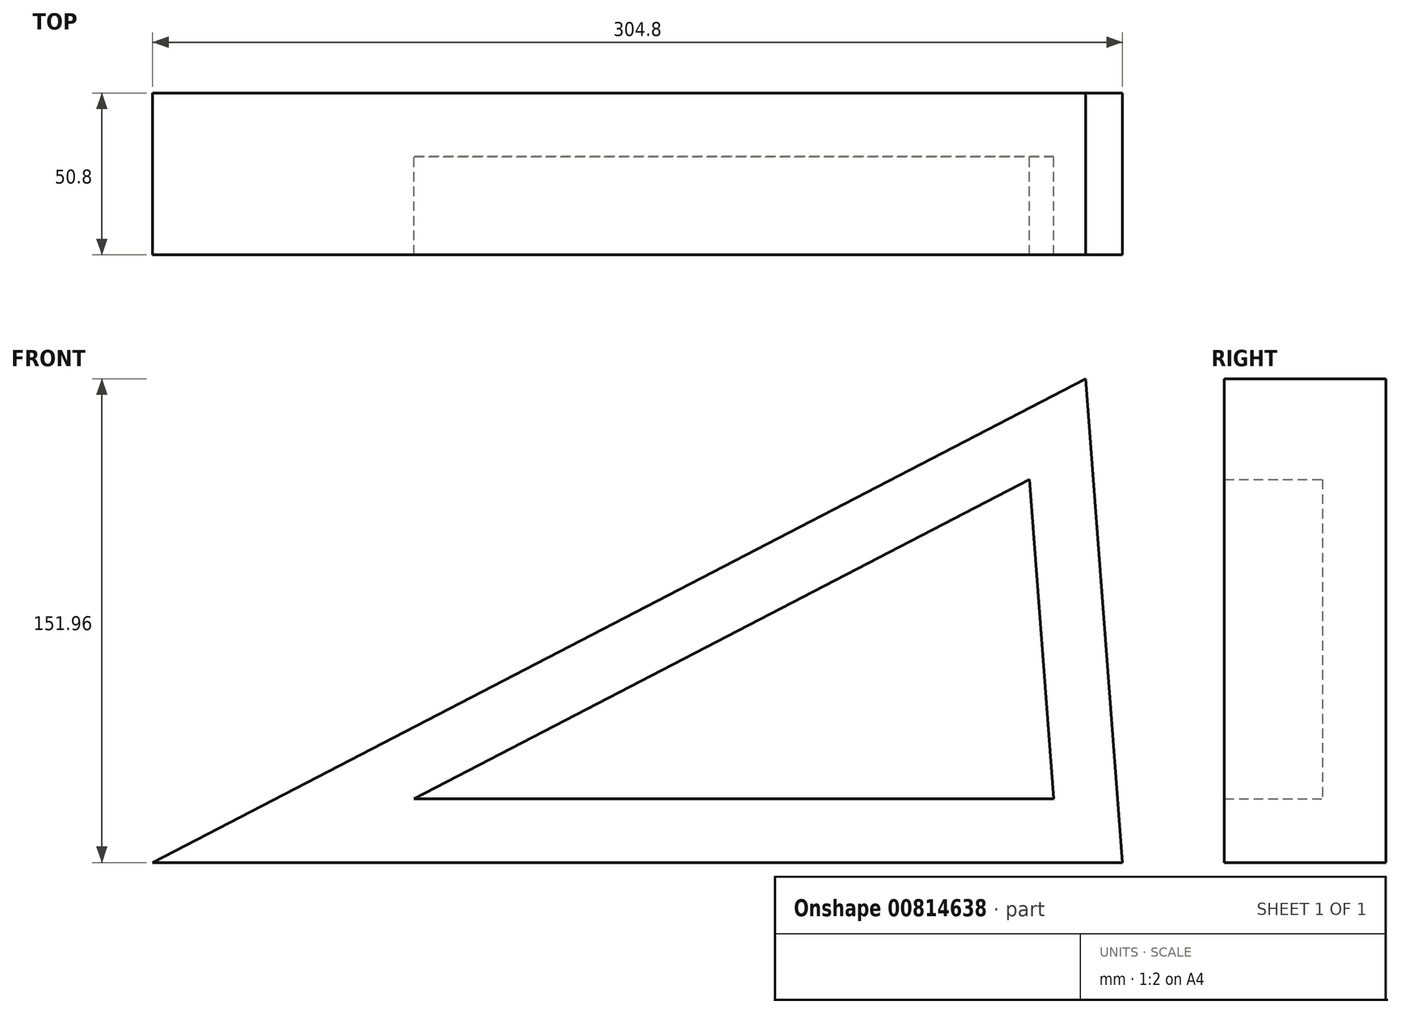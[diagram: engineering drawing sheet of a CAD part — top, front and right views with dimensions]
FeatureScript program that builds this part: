
annotation { "Feature Type Name" : "Feature", "Feature Type Description" : "" }
export const myFeature = defineFeature(function(context is Context, id is Id, definition is map)
    precondition{}
    {
        {
            var Q0;
            Q0=qCreatedBy(makeId("Front.planeOp"),FACE);
            var sketch = newSketch(context, id + "F0", { "sketchPlane" : qUnion([Q0])});
            skLineSegment(sketch, "E0.0", {"start": v(152.4, -87.99) * mm, "end": v(-152.4, -87.99) * mm});
            skLineSegment(sketch, "E0.1", {"start": v(-152.4, -87.99) * mm, "end": v(140.76, 63.97) * mm});
            skLineSegment(sketch, "E0.2", {"start": v(140.76, 63.97) * mm, "end": v(152.4, -87.99) * mm});
            skPoint(sketch, "E0.0.midPoint", {"position": v(0, -87.99) * mm});
            skPoint(sketch, "E0.cCircle.center.orphan", {"position": v(0, 0) * mm});
            skSolve(sketch);
        }
        {
            var Q0;
            Q0 = qSketchRegion(id + "F0", true);
            extrude(context, id + "F1", {"entities" : qUnion([Q0]), "depth" : 50.8 * mm, "offsetDistance" : 25.4 * mm});
        }
        {
            var Q0;
            Q0=makeQuery(id+"F1.opExtrude","CAP_FACE",FACE,{"disambiguationData":[OSD([sQuery(id+"F0.wireOp",EDGE,"E0.0"),sQuery(id+"F0.wireOp",EDGE,"E0.1"),sQuery(id+"F0.wireOp",EDGE,"E0.2")])],"isStart":false});
            shell(context, id + "F2", {"entities" : qUnion([Q0]), "thickness" : 20 * mm});
        }
    });
